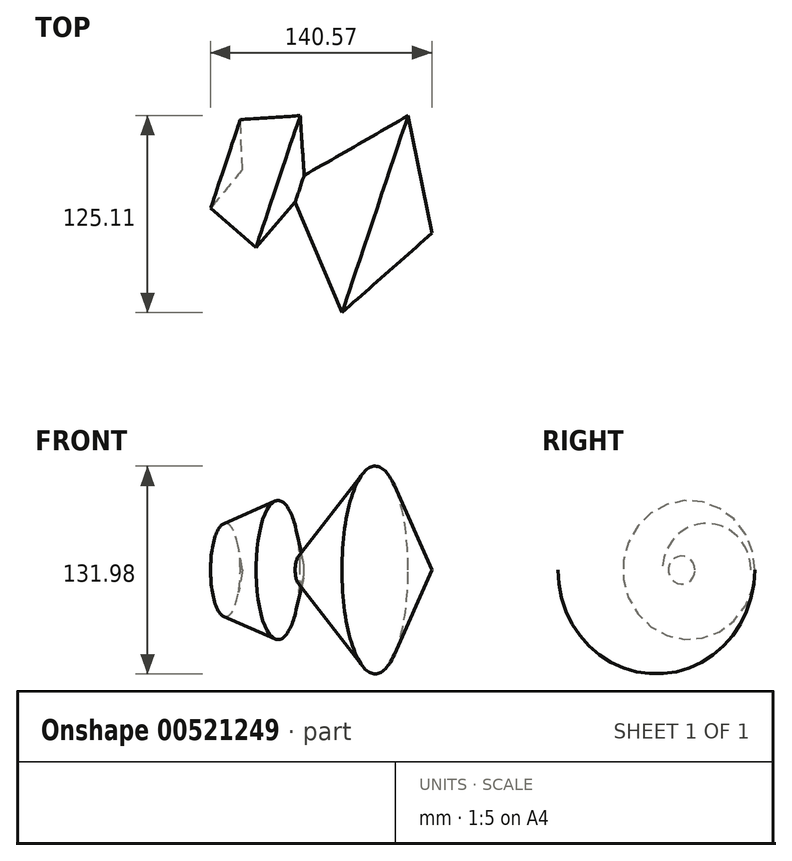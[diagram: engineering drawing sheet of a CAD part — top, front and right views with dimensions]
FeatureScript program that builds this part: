
annotation { "Feature Type Name" : "Feature", "Feature Type Description" : "" }
export const myFeature = defineFeature(function(context is Context, id is Id, definition is map)
    precondition{}
    {
        {
            var Q0;
            Q0=qCreatedBy(makeId("Top.planeOp"),FACE);
            var sketch = newSketch(context, id + "F0", { "sketchPlane" : qUnion([Q0])});
            skLineSegment(sketch, "E0", {"start": v(0, 0) * mm, "end": v(15.1, -74.69) * mm});
            skLineSegment(sketch, "E1", {"start": v(15.1, -74.69) * mm, "end": v(-105.29, -34.25) * mm});
            skLineSegment(sketch, "E2", {"start": v(-105.29, -34.25) * mm, "end": v(-106.58, -2.52) * mm});
            skLineSegment(sketch, "E3", {"start": v(-106.58, -2.52) * mm, "end": v(-68.56, 0) * mm});
            skLineSegment(sketch, "E4", {"start": v(-68.56, 0) * mm, "end": v(-66.04, -38.02) * mm});
            skLineSegment(sketch, "E5", {"start": v(-66.04, -38.02) * mm, "end": v(0, 0) * mm});
            skSolve(sketch);
        }
        {
            var Q0;
            Q0 = qSketchRegion(id + "F0", true);
            var Q1;
            Q1=sQuery(id+"F0.wireOp",EDGE,"E1");
            revolve(context, id + "F1", {"entities" : qUnion([Q0]), "axis" : qUnion([Q1]), "revolveType" : RevolveType.FULL});
        }
    });
